# Revit family: BESAM In Ground SW200i -IG Operator Center Pivot, Double Door
name_source: partatom
category: Generic Models
revit_build: Autodesk Revit 2014 (Build: 20130308_1515(x64)
units: mm (PartAtom-declared; Revit-internal decimal feet)

## types (1)
- BESAM In Ground SW200i -IG Operator Center Pivot, Double Door
    Additional Equipment Required = SW200i-IG In Ground Operator requires purchase of SW200i Operator, a SW200i-IG installation kit and an Output Shaft Adaptor. Doors, door arms and threshold by others.
    BIMobject category = Swing Doors
    Date of publishing = 2015-02-23
    Description = Reliable in ground mounting, single or pair applications, with moisture resistant and splash proof mounting case. Multiple arm configurations, new construction or modernization to existing equipment, air pressure management, manual push forces of 5- 15 lbf
    Door Pivot = Besam Center Pivot included if selected.
    Door Width = 76 "
    Edition number = 1
    Floating Door Pivot = Metal, Powder Coated, Black
    IFC Classification = Door
    In Ground Enclosure = The SW200i-IG enclosure is splash proof when correctly assembled. Finish of IG Enclosure is Black Powder Coat suitable for masonry exposure. All exterior hardware is Stainless Steel. It is essential the pit is drained or provided with a sump pump to prevent water accumulation in the pit.
    Main Material = Stainless Steel, Polished
    Manufacturer name = Besam-North America
    Material main = Aluminium
    Max Door Weight = 700.00 lbf
    Min Door Width = 76 "
    Mounting Pit Width = 8 "
    Nominal height = 0
    Nominal width = 0
    Output Shaft Adaptor = Besam SW200i-IG Installation Manual 1009955
    Pit Depth = 7 "
    Power/Reset Switch = SW200i Power/Reset switch is mounted within th e In Ground enclosure. Alternative optional Switch mounting for 3 position on/off/hold, or 4 position off/two way/one-way/hold will be required on the door frame or optional remote box.
    Product Application = The SW200i-IG In Ground Operator is designed for pedestrian and ADA applications that require manual push forces to comply with ANSI 156.19 and fire door regulations.
    Product Guid = 7c94be0d-9701-4848-a405-2ff074569a87
    Product SKU = SW200i-IG
    Product data url = http://bimobject.com
    Product family = Swing
    Product group = In-ground
    QR code = http://bimobject.com
    Secondary Material = Metal, Powder Coated, Black
    Threshold Thickness = 1 "
    Threshold Width = 10 "
    UNSPSC Code = 30171511
    Uniclass 1.4 Code = L81323
    Uniclass 1.4 Description = Swings
    Weight Net (Kg) = 0

## geometry (parser evidence)
native form markers: Sweep x2
no freeform markers — native parametric forms only
